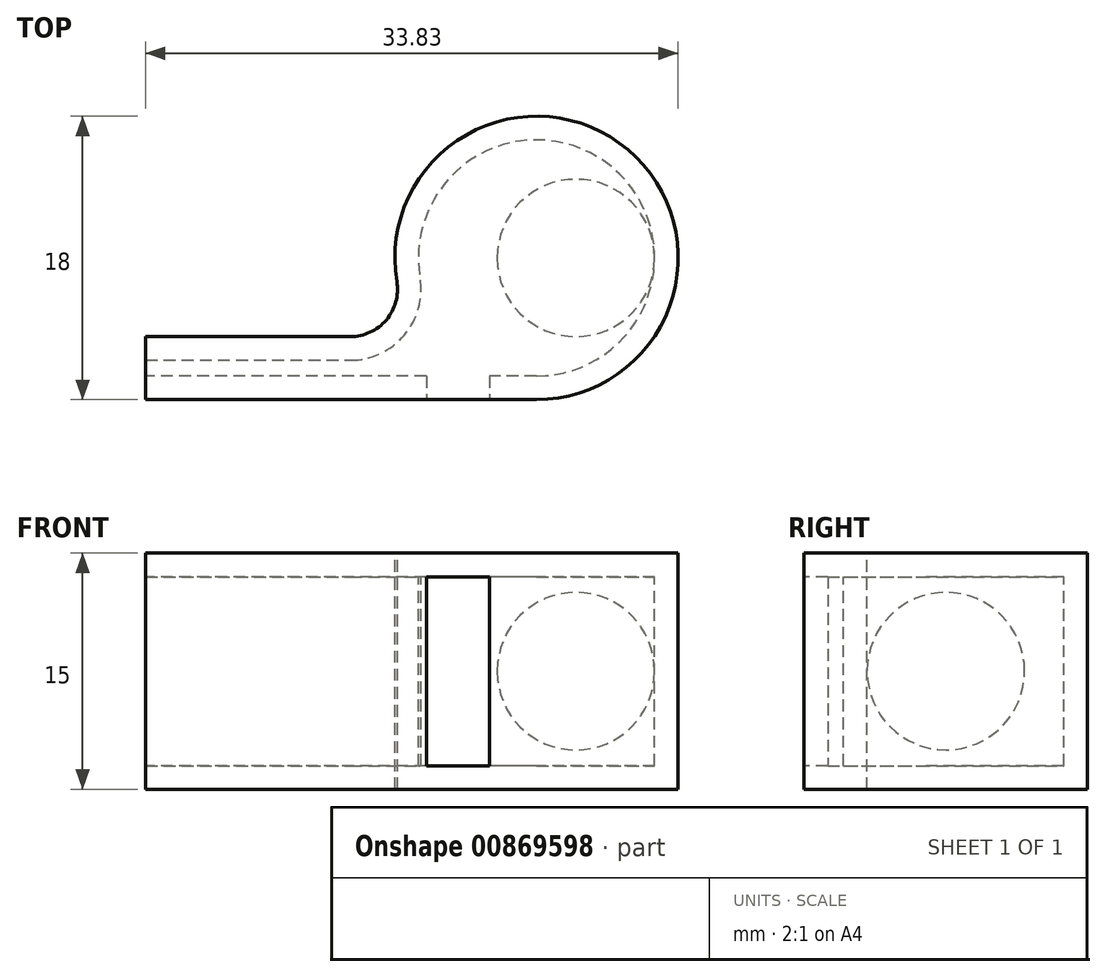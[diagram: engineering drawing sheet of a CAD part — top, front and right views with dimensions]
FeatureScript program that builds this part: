
annotation { "Feature Type Name" : "Feature", "Feature Type Description" : "" }
export const myFeature = defineFeature(function(context is Context, id is Id, definition is map)
    precondition{}
    {
        {
            var Q0;
            Q0=qCreatedBy(makeId("Top.planeOp"),FACE);
            var sketch = newSketch(context, id + "F0", { "sketchPlane" : qUnion([Q0])});
            skArc(sketch, "E0", {"start": v(0, -9) * mm, "mid": v(5.8, 6.87) * mm, "end": v(-8.87, -1.5) * mm});
            skLineSegment(sketch, "E1", {"start": v(0, -9) * mm, "end": v(-24.83, -9) * mm});
            skLineSegment(sketch, "E2", {"start": v(-24.83, -9) * mm, "end": v(-24.83, -5) * mm});
            skLineSegment(sketch, "E3", {"start": v(-24.83, -5) * mm, "end": v(-11.83, -5) * mm});
            skPoint(sketch, "E4.visualSharp", {"position": v(-7.48, -5) * mm});
            skArc(sketch, "E4.filletArc", {"start": v(-11.83, -5) * mm, "mid": v(-9.54, -3.94) * mm, "end": v(-8.87, -1.5) * mm});
            skSolve(sketch);
        }
        {
            var Q0;
            Q0=makeQuery(id+"F0.imprint","IMPRINT",FACE,{"disambiguationData":[TD([[makeQuery(id+"F0.imprint","IMPRINT",EDGE,{"derivedFrom":sQuery(id+"F0.wireOp",EDGE,"E0")}),1.0]])]});
            extrude(context, id + "F1", {"entities" : qUnion([Q0]), "endBound" : BoundingType.SYMMETRIC, "oppositeDirection" : true, "depth" : 15 * mm, "offsetDistance" : 25 * mm});
        }
        {
            var Q0;
            Q0=makeQuery(id+"F1.opExtrude","SWEPT_FACE",FACE,{"disambiguationData":[OSD([sQuery(id+"F0.wireOp",EDGE,"E2")])]});
            shell(context, id + "F2", {"entities" : qUnion([Q0]), "thickness" : 1.5 * mm});
        }
        {
            var Q0;
            Q0=makeQuery(id+"F1.opExtrude","SWEPT_FACE",FACE,{"disambiguationData":[OSD([sQuery(id+"F0.wireOp",EDGE,"E1")])]});
            var sketch = newSketch(context, id + "F3", { "sketchPlane" : qUnion([Q0])});
            skLineSegment(sketch, "E5.bottom", {"start": v(-7, -6) * mm, "end": v(-3, -6) * mm});
            skLineSegment(sketch, "E5.top", {"start": v(-7, 6) * mm, "end": v(-3, 6) * mm});
            skLineSegment(sketch, "E5.left", {"start": v(-7, 6) * mm, "end": v(-7, -6) * mm});
            skLineSegment(sketch, "E5.right", {"start": v(-3, 6) * mm, "end": v(-3, -6) * mm});
            skSolve(sketch);
        }
        {
            var Q0;
            Q0=makeQuery(id+"F3.imprint","IMPRINT",FACE,{"disambiguationData":[TD([[makeQuery(id+"F3.imprint","IMPRINT",EDGE,{"derivedFrom":sQuery(id+"F3.wireOp",EDGE,"E5.bottom")}),1.0]])]});
            extrude(context, id + "F4", {"entities" : qUnion([Q0]), "operationType" : NewBodyOperationType.REMOVE, "oppositeDirection" : true, "depth" : 1.5 * mm, "offsetDistance" : 25 * mm});
        }
        {
            var Q0;
            Q0=qCreatedBy(makeId("Top.planeOp"),FACE);
            var sketch = newSketch(context, id + "F5", { "sketchPlane" : qUnion([Q0])});
            skArc(sketch, "E6", {"start": v(-2.5, 0) * mm, "mid": v(2.5, 5) * mm, "end": v(7.5, 0) * mm});
            skLineSegment(sketch, "E7", {"start": v(-2.5, 0) * mm, "end": v(7.5, 0) * mm});
            skSolve(sketch);
        }
        {
            var Q0;
            Q0 = qSketchRegion(id + "F5", true);
            var Q1;
            Q1=sQuery(id+"F5.wireOp",EDGE,"E7");
            revolve(context, id + "F6", {"surfaceOperationType" : NewSurfaceOperationType.NEW, "entities" : qUnion([Q0]), "axis" : qUnion([Q1]), "revolveType" : RevolveType.FULL});
        }
    });
